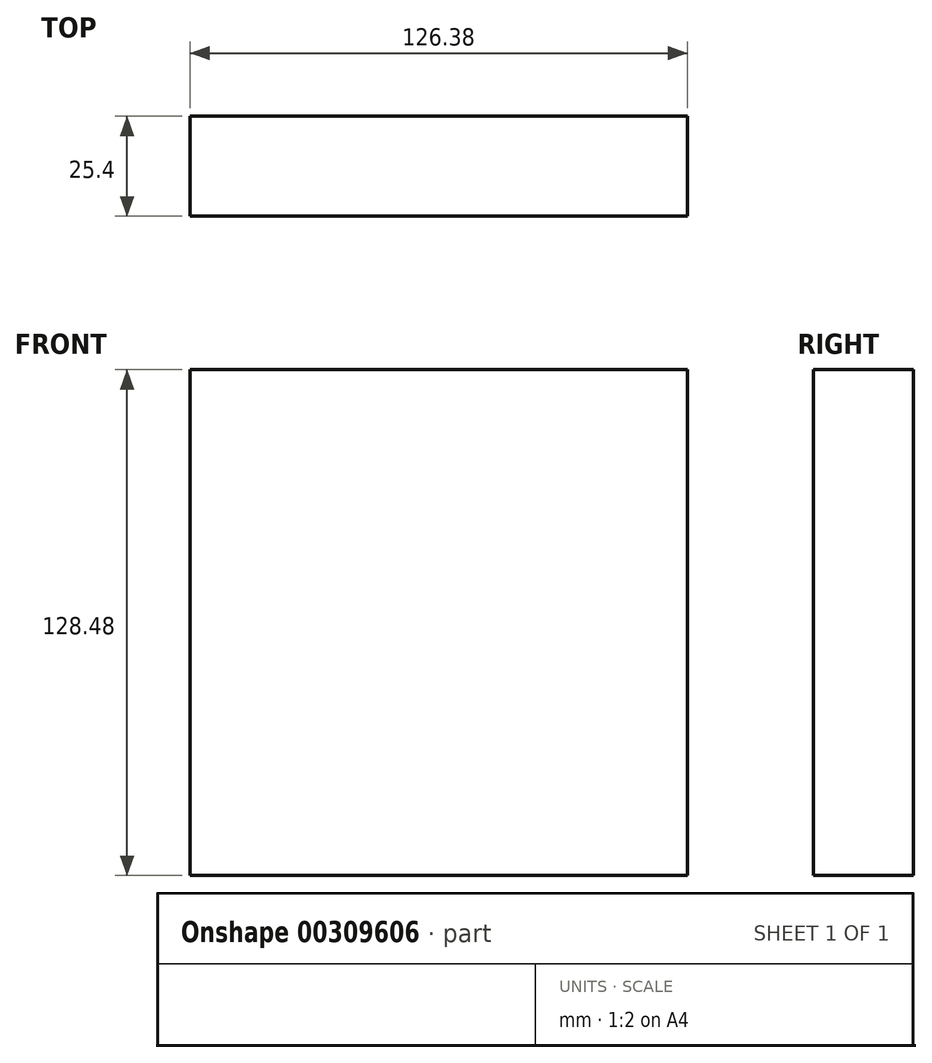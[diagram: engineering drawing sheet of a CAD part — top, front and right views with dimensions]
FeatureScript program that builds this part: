
annotation { "Feature Type Name" : "Feature", "Feature Type Description" : "" }
export const myFeature = defineFeature(function(context is Context, id is Id, definition is map)
    precondition{}
    {
        {
            var Q0;
            Q0=qCreatedBy(makeId("Front.planeOp"),FACE);
            var sketch = newSketch(context, id + "F0", { "sketchPlane" : qUnion([Q0])});
            skLineSegment(sketch, "E0.bottom", {"start": v(63.2, 64.24) * mm, "end": v(-63.2, 64.24) * mm});
            skLineSegment(sketch, "E0.top", {"start": v(63.2, -64.24) * mm, "end": v(-63.2, -64.24) * mm});
            skLineSegment(sketch, "E0.left", {"start": v(63.2, 64.24) * mm, "end": v(63.2, -64.24) * mm});
            skLineSegment(sketch, "E0.right", {"start": v(-63.2, 64.24) * mm, "end": v(-63.2, -64.24) * mm});
            skPoint(sketch, "E0.middle", {"position": v(0, 0) * mm});
            skSolve(sketch);
        }
        {
            var Q0;
            Q0 = qSketchRegion(id + "F0", true);
            extrude(context, id + "F1", {"entities" : qUnion([Q0]), "depth" : 25.4 * mm});
        }
    });
